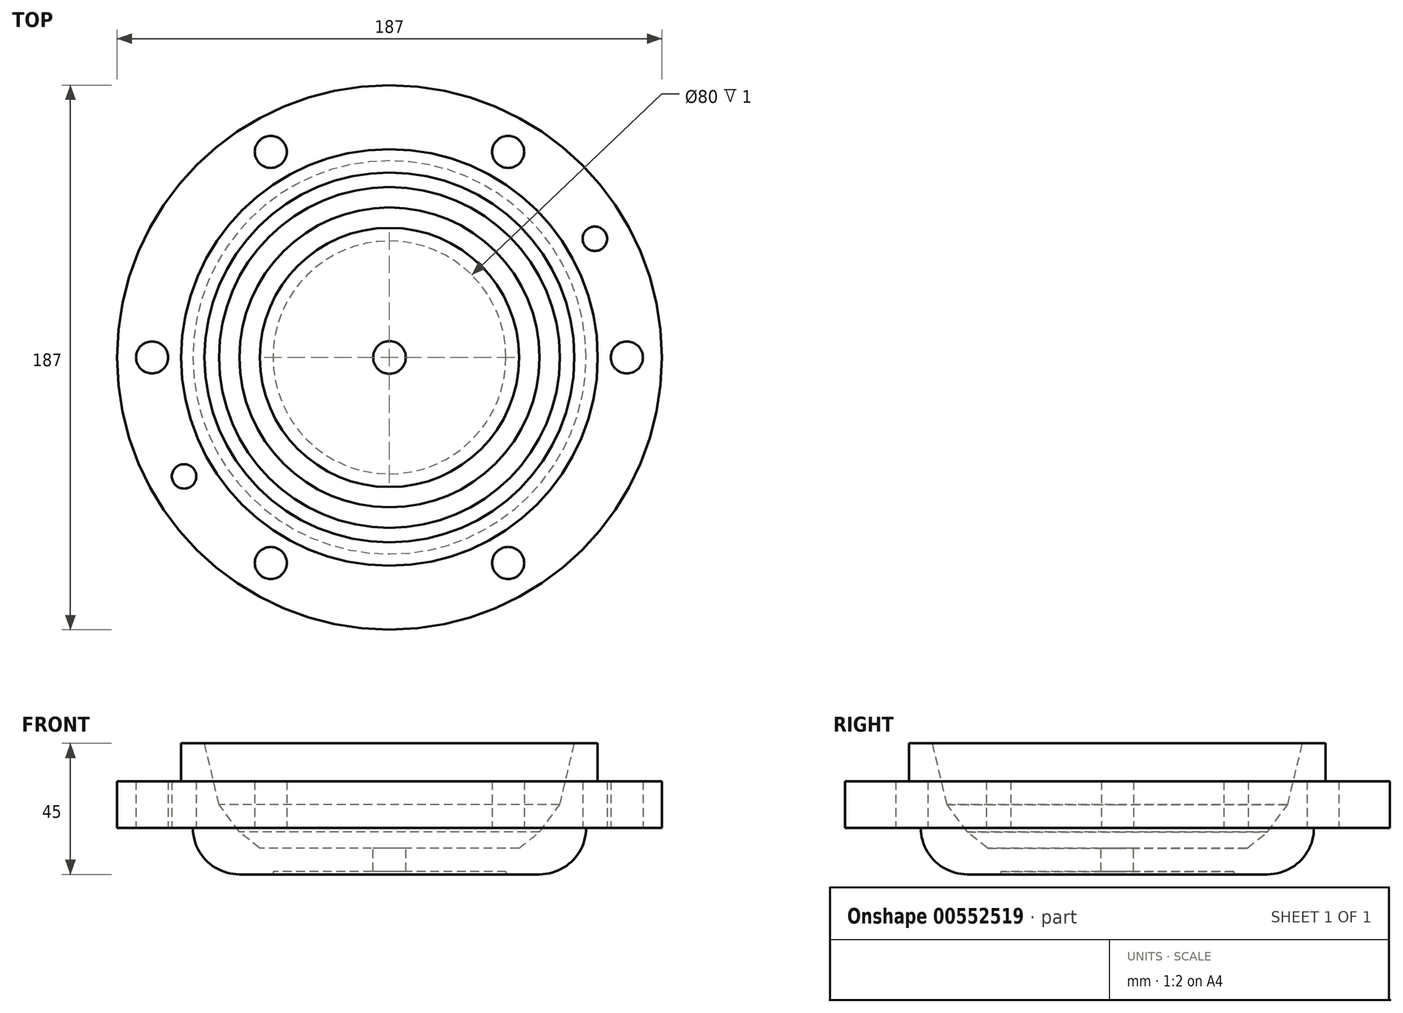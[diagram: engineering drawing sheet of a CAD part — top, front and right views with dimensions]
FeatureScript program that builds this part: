
annotation { "Feature Type Name" : "Feature", "Feature Type Description" : "" }
export const myFeature = defineFeature(function(context is Context, id is Id, definition is map)
    precondition{}
    {
        {
            var Q0;
            Q0=qCreatedBy(makeId("Top.planeOp"),FACE);
            var sketch = newSketch(context, id + "F0", { "sketchPlane" : qUnion([Q0])});
            skCircle(sketch, "E0", {"center": v(0, 0) * mm, "radius": 93.5 * mm});
            skCircle(sketch, "E1", {"center": v(-81.5, 0) * mm, "radius": 5.5 * mm});
            skCircle(sketch, "E2.1.0", {"center": v(-40.75, -70.58) * mm, "radius": 5.5 * mm});
            skCircle(sketch, "E2.2.0", {"center": v(40.75, -70.58) * mm, "radius": 5.5 * mm});
            skCircle(sketch, "E2.3.0", {"center": v(81.5, 0) * mm, "radius": 5.5 * mm});
            skCircle(sketch, "E2.4.0", {"center": v(40.75, 70.58) * mm, "radius": 5.5 * mm});
            skCircle(sketch, "E2.5.0", {"center": v(-40.75, 70.58) * mm, "radius": 5.5 * mm});
            skCircle(sketch, "E3", {"center": v(0, 0) * mm, "radius": 71.5 * mm});
            skCircle(sketch, "E4", {"center": v(0, 0) * mm, "radius": 67.5 * mm});
            skCircle(sketch, "E5", {"center": v(0, 0) * mm, "radius": 40 * mm});
            skCircle(sketch, "E6", {"center": v(0, 0) * mm, "radius": 5.6 * mm});
            skCircle(sketch, "E7", {"center": v(70.52, 40.75) * mm, "radius": 4.2 * mm});
            skCircle(sketch, "E8.MirrorC", {"center": v(-70.52, -40.85) * mm, "radius": 4.2 * mm});
            skSolve(sketch);
        }
        {
            var Q0;
            Q0=makeQuery(id+"F0.imprint","IMPRINT",FACE,{"disambiguationData":[TD([[makeQuery(id+"F0.imprint","IMPRINT",EDGE,{"derivedFrom":sQuery(id+"F0.wireOp",EDGE,"E0")}),1.0]])]});
            extrude(context, id + "F1", {"entities" : qUnion([Q0]), "depth" : 16 * mm, "offsetDistance" : 25 * mm});
        }
        {
            var Q0;
            Q0=makeQuery(id+"F0.imprint","IMPRINT",FACE,{"disambiguationData":[TD([[makeQuery(id+"F0.imprint","IMPRINT",EDGE,{"derivedFrom":sQuery(id+"F0.wireOp",EDGE,"E4")}),1.0]])]});
            var Q1;
            Q1=makeQuery(id+"F0.imprint","IMPRINT",FACE,{"disambiguationData":[TD([[makeQuery(id+"F0.imprint","IMPRINT",EDGE,{"derivedFrom":sQuery(id+"F0.wireOp",EDGE,"E3")}),1.0]])]});
            extrude(context, id + "F2", {"entities" : qUnion([Q0, Q1]), "operationType" : NewBodyOperationType.ADD, "depth" : 29 * mm, "offsetDistance" : 25 * mm});
        }
        {
            var Q0;
            Q0=makeQuery(id+"F0.imprint","IMPRINT",FACE,{"disambiguationData":[TD([[makeQuery(id+"F0.imprint","IMPRINT",EDGE,{"derivedFrom":sQuery(id+"F0.wireOp",EDGE,"E4")}),1.0]])]});
            extrude(context, id + "F3", {"entities" : qUnion([Q0]), "operationType" : NewBodyOperationType.ADD, "oppositeDirection" : true, "depth" : 16 * mm, "offsetDistance" : 25 * mm});
        }
        {
            var Q0;
            Q0=makeQuery(id+"F3.opExtrude","CAP_EDGE",EDGE,{"disambiguationData":[OSD([sQuery(id+"F0.wireOp",EDGE,"E4")])],"isStart":false});
            fillet(context, id + "F4", {"entities" : qUnion([Q0]), "radius" : 16 * mm, "tangentPropagation" : true, "allowEdgeOverflow" : false});
        }
        {
            var Q0;
            Q0=makeQuery(id+"F0.imprint","IMPRINT",FACE,{"disambiguationData":[TD([[makeQuery(id+"F0.imprint","IMPRINT",EDGE,{"derivedFrom":sQuery(id+"F0.wireOp",EDGE,"E5")}),1.0]])]});
            extrude(context, id + "F5", {"entities" : qUnion([Q0]), "operationType" : NewBodyOperationType.ADD, "oppositeDirection" : true, "depth" : 15 * mm, "offsetDistance" : 25 * mm});
        }
        {
            var Q0;
            Q0=qCreatedBy(makeId("Front.planeOp"),FACE);
            var sketch = newSketch(context, id + "F6", { "sketchPlane" : qUnion([Q0])});
            skLineSegment(sketch, "E9", {"start": v(0, 8) * mm, "end": v(58.5, 8) * mm});
            skLineSegment(sketch, "E10", {"start": v(0, 8) * mm, "end": v(0, 29) * mm});
            skLineSegment(sketch, "E11", {"start": v(0, 29) * mm, "end": v(63.5, 29) * mm});
            skLineSegment(sketch, "E12", {"start": v(63.5, 29) * mm, "end": v(58.5, 8) * mm});
            skSolve(sketch);
        }
        {
            var Q0;
            Q0=makeQuery(id+"F6.imprint","IMPRINT",FACE,{"disambiguationData":[TD([[makeQuery(id+"F6.imprint","IMPRINT",EDGE,{"derivedFrom":sQuery(id+"F6.wireOp",EDGE,"E9")}),1.0]])]});
            var Q1;
            Q1=sQuery(id+"F6.wireOp",EDGE,"E10");
            var Q2;
            Q2=sQuery(id+"F6.wireOp",EDGE,"E11");
            var Q3;
            Q3=sQuery(id+"F6.wireOp",EDGE,"E12");
            var Q4;
            Q4=sQuery(id+"F6.wireOp",EDGE,"E9");
            var Q5;
            Q5=sQuery(id+"F6.wireOp",EDGE,"E10");
            revolve(context, id + "F7", {"operationType" : NewBodyOperationType.REMOVE, "entities" : qUnion([Q0]), "surfaceEntities" : qUnion([Q1, Q2, Q3, Q4]), "axis" : qUnion([Q5]), "revolveType" : RevolveType.FULL, "oppositeDirection" : true});
        }
        {
            var Q0;
            Q0=qCreatedBy(makeId("Front.planeOp"),FACE);
            var sketch = newSketch(context, id + "F8", { "sketchPlane" : qUnion([Q0])});
            skLineSegment(sketch, "E13", {"start": v(51.5, -1.5) * mm, "end": v(58.5, 8) * mm});
            skLineSegment(sketch, "E14", {"start": v(58.5, 8) * mm, "end": v(0, 8) * mm});
            skLineSegment(sketch, "E15", {"start": v(0, -1.5) * mm, "end": v(0, 8) * mm});
            skLineSegment(sketch, "E16", {"start": v(0, -1.5) * mm, "end": v(0, -7) * mm});
            skLineSegment(sketch, "E17", {"start": v(0, -7) * mm, "end": v(44.5, -7) * mm});
            skLineSegment(sketch, "E18", {"start": v(44.5, -7) * mm, "end": v(51.5, -1.5) * mm});
            skSolve(sketch);
        }
        {
            var Q0;
            Q0=makeQuery(id+"F8.imprint","IMPRINT",FACE,{"disambiguationData":[TD([[makeQuery(id+"F8.imprint","IMPRINT",EDGE,{"derivedFrom":sQuery(id+"F8.wireOp",EDGE,"E13")}),1.0]])]});
            var Q1;
            Q1=sQuery(id+"F8.wireOp",EDGE,"E15");
            revolve(context, id + "F9", {"operationType" : NewBodyOperationType.REMOVE, "entities" : qUnion([Q0]), "axis" : qUnion([Q1]), "revolveType" : RevolveType.FULL, "oppositeDirection" : true});
        }
    });
